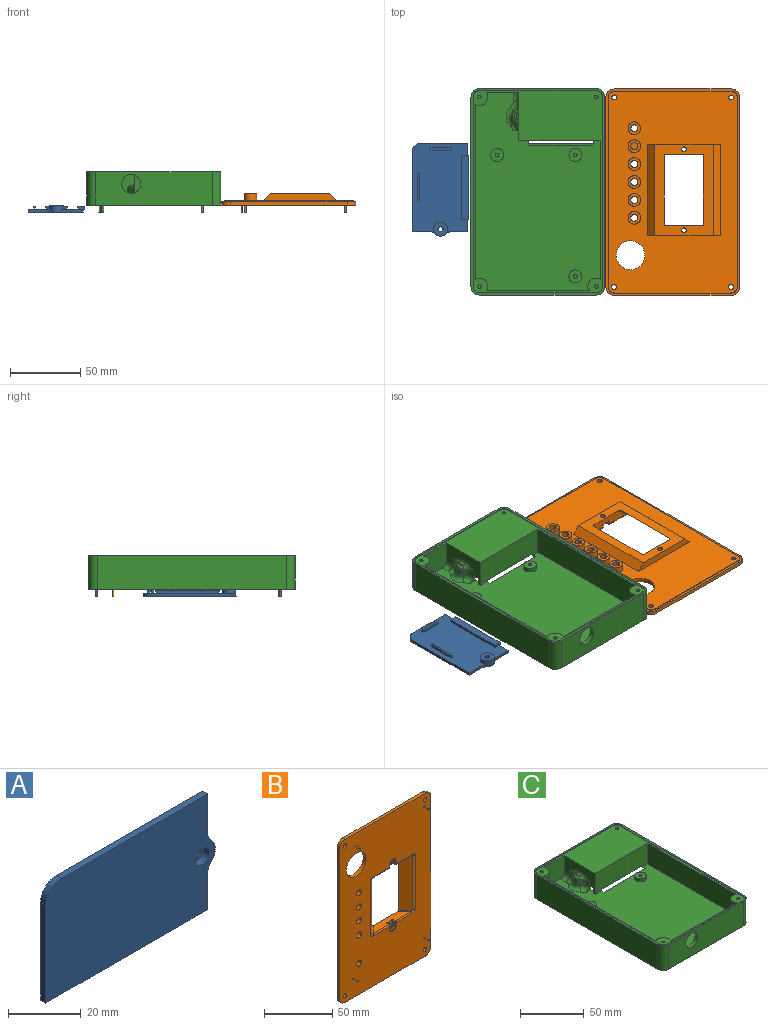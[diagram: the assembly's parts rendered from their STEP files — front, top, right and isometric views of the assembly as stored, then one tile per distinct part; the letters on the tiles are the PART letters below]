
ASSEMBLY  parts=3 mates=2
PART A: 31 faces, bbox 66x5x40 mm
  f0: plane 64.5x39mm, normal (0,1,0), area 2157.2mm2, adj f2,f3,f4,f5,f6,f7,f8,f9
  f1: cylinder r=1.75mm len=3.5mm, axis (0,-1,0), area 29.7mm2, adj f12,f13
  f2: cylinder r=5mm len=3.57mm, axis (0,1,0), area 8mm2, adj f0,f3,f10,f11
  f3: cylinder r=5mm len=10mm, axis (0,1,0), area 110.2mm2, adj f0,f2,f4,f11,f12
  f4: cylinder r=5mm len=3.57mm, axis (0,1,0), area 8mm2, adj f0,f3,f5,f11
  f5: plane 12.86x2mm, normal (1,0,0), area 25.7mm2, adj f0,f4,f6,f11
  f6: plane 57x2mm, normal (0,0,1), area 114mm2, adj f0,f5,f7,f11
  f7: cylinder r=6mm len=6mm, axis (0,1,0), area 18.8mm2, adj f0,f6,f8,f11
  f8: plane 33x2mm, normal (-1,0,0), area 66mm2, adj f0,f7,f9,f11
  f9: plane 63x2mm, normal (0,0,-1), area 126mm2, adj f0,f8,f10,f11,f25
  f10: plane 11.86x2mm, normal (1,0,0), area 23.7mm2, adj f0,f2,f9,f11
  f11: plane 66x39mm, normal (0,-1,0), area 2446.5mm2, adj f2,f3,f4,f5,f6,f7,f8,f9
  f12: plane 10x10mm, normal (0,1,0), area 68.9mm2, adj f1,f3
  f13: plane 5.55x5.55mm, normal (0,-1,0), area 14.6mm2, adj f1,f14
  f14: cylinder r=2.77mm len=5.55mm, axis (0,-1,0), area 40.1mm2, adj f11,f13
  f15: plane 2x1.25mm, normal (1,0,0), area 2.5mm2, adj f0,f16,f18,f19
  f16: plane 20x2mm, normal (0,0,-1), area 40mm2, adj f0,f15,f17,f19
  f17: plane 2x1.25mm, normal (-1,0,0), area 2.5mm2, adj f0,f16,f18,f19
  f18: plane 20x2mm, normal (0,0,1), area 40mm2, adj f0,f15,f17,f19
  f19: plane 20x1.25mm, normal (0,1,0), area 25mm2, adj f15,f16,f17,f18
  f20: plane 15x2mm, normal (-1,0,0), area 30mm2, adj f0,f21,f23,f24
  f21: plane 2x2mm, normal (0,0,1), area 4mm2, adj f0,f20,f22,f24
  f22: plane 15x2mm, normal (1,0,0), area 30mm2, adj f0,f21,f23,f24
  f23: plane 2x2mm, normal (0,0,-1), area 4mm2, adj f0,f20,f22,f24
  f24: plane 15x2mm, normal (0,1,0), area 30mm2, adj f20,f21,f22,f23
  f25: plane 45x0.95mm, normal (0,-1,0), area 42.8mm2, adj f9,f26,f27,f30
  f26: plane 4.95x2mm, normal (-1,0,0), area 9.9mm2, adj f0,f25,f28,f29,f30
  f27: plane 4.95x2mm, normal (1,0,0), area 9.9mm2, adj f0,f25,f28,f29,f30
  f28: plane 45x4.95mm, normal (0,1,0), area 222.7mm2, adj f26,f27,f29,f30
  f29: plane 45x2mm, normal (0,0,1), area 90mm2, adj f0,f26,f27,f28
  f30: plane 45x2mm, normal (0,0,-1), area 90mm2, adj f25,f26,f27,f28
PART B: 118 faces, bbox 95.4x14.1x146.9 mm
  f0: plane 143.15x91.65mm, normal (0,1,0), area 9009.7mm2, adj f22,f23,f25,f27,f29,f31,f33,f35
  f1: cylinder r=1mm len=15.99mm, axis (1,0,0), area 25.1mm2, adj f5,f19,f47,f70
  f2: cylinder r=1mm len=15.99mm, axis (-1,0,0), area 25.1mm2, adj f5,f20,f50,f82
  f3: cylinder r=1.75mm len=5mm, axis (0,-1,0), area 55mm2, adj f21,f59
  f4: cylinder r=1.75mm len=5mm, axis (0,-1,0), area 55mm2, adj f21,f53
  f5: plane 146.66x95.16mm, normal (0,-1,0), area 10918.9mm2, adj f1,f2,f6,f7,f8,f9,f10,f11
  f6: cylinder r=6mm len=6mm, axis (0,1,0), area 23.6mm2, adj f5,f7,f13,f93
  f7: plane 83x2.5mm, normal (0,0,1), area 207.5mm2, adj f5,f6,f8,f93
  f8: cylinder r=6mm len=6mm, axis (0,1,0), area 23.6mm2, adj f5,f7,f9,f93
  f9: plane 134.5x2.5mm, normal (-1,0,0), area 336.2mm2, adj f5,f8,f10,f93
  f10: cylinder r=6mm len=6mm, axis (0,1,0), area 23.6mm2, adj f5,f9,f11,f93
  f11: plane 83x2.5mm, normal (0,0,-1), area 207.5mm2, adj f5,f10,f12,f93
  f12: cylinder r=6mm len=6mm, axis (0,1,0), area 23.6mm2, adj f5,f11,f13,f93
  f13: plane 134.5x2.5mm, normal (1,0,0), area 336.2mm2, adj f5,f6,f12,f93
  f14: cylinder r=2.5mm len=8mm, axis (0,1,0), area 125.7mm2, adj f5,f32
  f15: cylinder r=2.5mm len=8mm, axis (0,1,0), area 125.7mm2, adj f5,f30
  f16: cylinder r=2.5mm len=8mm, axis (0,1,0), area 125.7mm2, adj f5,f28
  f17: cylinder r=2.5mm len=8mm, axis (0,1,0), area 125.7mm2, adj f5,f26
  f18: cylinder r=2.5mm len=8mm, axis (0,1,0), area 125.7mm2, adj f5,f24
  f19: plane 38.77x7mm, normal (0,0,-1), area 205.8mm2, adj f1,f21,f40,f44,f45,f64,f65,f66
  f20: plane 38.77x7mm, normal (0,0,1), area 205.8mm2, adj f2,f21,f42,f48,f51,f77,f78,f79
  f21: plane 65.22x42.02mm, normal (0,1,0), area 1275.6mm2, adj f3,f4,f19,f20,f22,f23,f38,f39
  f22: plane 51.6x5mm, normal (0,0,1), area 233mm2, adj f0,f21,f87,f88
  f23: plane 51.6x5mm, normal (0,0,-1), area 233mm2, adj f0,f21,f87,f88
  f24: plane 9x9mm, normal (0,1,0), area 44mm2, adj f18,f25
  f25: cylinder r=4.5mm len=9mm, axis (0,-1,0), area 141.4mm2, adj f0,f24
  f26: plane 9x9mm, normal (0,1,0), area 44mm2, adj f17,f27
  f27: cylinder r=4.5mm len=9mm, axis (0,-1,0), area 141.4mm2, adj f0,f26
  f28: plane 9x9mm, normal (0,1,0), area 44mm2, adj f16,f29
  f29: cylinder r=4.5mm len=9mm, axis (0,-1,0), area 141.4mm2, adj f0,f28
  f30: plane 9x9mm, normal (0,1,0), area 44mm2, adj f15,f31
  f31: cylinder r=4.5mm len=9mm, axis (0,-1,0), area 141.4mm2, adj f0,f30
  f32: plane 9x9mm, normal (0,1,0), area 44mm2, adj f14,f33
  f33: cylinder r=4.5mm len=9mm, axis (0,-1,0), area 141.4mm2, adj f0,f32
  f34: plane 9x9mm, normal (0,1,0), area 44mm2, adj f35,f36
  f35: cylinder r=4.5mm len=9mm, axis (0,-1,0), area 141.4mm2, adj f0,f34
  f36: cylinder r=2.5mm len=5mm, axis (0,-1,0), area 78.5mm2, adj f34,f37
  f37: plane 5x5mm, normal (0,1,0), area 19.6mm2, adj f36
  f38: plane 48.8x7.12mm, normal (-0.71,-0.71,0), area 491.5mm2, adj f21,f40,f42,f43
  f39: plane 48.8x7.12mm, normal (0.71,-0.71,0), area 491.5mm2, adj f21,f45,f49,f51
  f40: cylinder r=1mm len=8.54mm, axis (0.71,-0.71,0), area 15.7mm2, adj f19,f21,f38,f41
  f41: bspline ~3.66x2.02mm, area 6.2mm2, adj f5,f40,f43,f44
  f42: cylinder r=1mm len=8.54mm, axis (-0.71,0.71,0), area 15.7mm2, adj f20,f21,f38,f46
  f43: cylinder r=3mm len=48.8mm, axis (0,0,-1), area 115mm2, adj f5,f38,f41,f46
  f44: cylinder r=1mm len=15.99mm, axis (1,0,0), area 25.1mm2, adj f5,f19,f41,f69
  f45: cylinder r=1mm len=8.54mm, axis (0.71,0.71,0), area 15.7mm2, adj f19,f21,f39,f47
  f46: bspline ~3.66x2.02mm, area 6.2mm2, adj f5,f42,f43,f48
  f47: bspline ~3.66x2.02mm, area 6.2mm2, adj f1,f5,f45,f49
  f48: cylinder r=1mm len=15.99mm, axis (-1,0,0), area 25.1mm2, adj f5,f20,f46,f83
  f49: cylinder r=3mm len=48.8mm, axis (0,0,1), area 115mm2, adj f5,f39,f47,f50
  f50: bspline ~3.66x2.02mm, area 6.2mm2, adj f2,f5,f49,f51
  f51: cylinder r=1mm len=8.54mm, axis (-0.71,-0.71,0), area 15.7mm2, adj f20,f21,f39,f50
  f52: cylinder r=10.25mm len=20.5mm, axis (0,-1,0), area 193.2mm2, adj f0,f5
  f53: plane 5.25x4.8mm, normal (0,-1,0), area 13.1mm2, adj f4,f61,f62,f63,f64
  f54: plane 2.85x2mm, normal (-1,0,0), area 5.6mm2, adj f56,f62,f67,f69,f71
  f55: plane 2.85x2mm, normal (1,0,0), area 5.6mm2, adj f56,f63,f68,f70,f72
  f56: cylinder r=2.9mm len=5.8mm, axis (0,-1,0), area 18.2mm2, adj f54,f55,f61,f73
  f57: plane 2.85x2mm, normal (1,0,0), area 5.6mm2, adj f60,f75,f80,f82,f84
  f58: plane 2.85x2mm, normal (-1,0,0), area 5.6mm2, adj f60,f76,f81,f83,f85
  f59: plane 5.25x4.8mm, normal (0,-1,0), area 13.1mm2, adj f3,f74,f75,f76,f77
  f60: cylinder r=2.9mm len=5.8mm, axis (0,-1,0), area 18.2mm2, adj f57,f58,f74,f86
  f61: torus R=2.4mm, axis (0,-1,0), area 6.7mm2, adj f53,f56,f62,f63
  f62: cylinder r=0.5mm len=2.85mm, axis (0,0,1), area 2.2mm2, adj f53,f54,f61,f65
  f63: cylinder r=0.5mm len=2.85mm, axis (0,0,-1), area 2.2mm2, adj f53,f55,f61,f66
  f64: cylinder r=0.5mm len=4.8mm, axis (-1,0,0), area 3.8mm2, adj f19,f53,f65,f66
  f65: torus R=1mm, axis (0,0,1), area 0.8mm2, adj f19,f62,f64,f67
  f66: torus R=1mm, axis (0,0,1), area 0.8mm2, adj f19,f63,f64,f68
  f67: cylinder r=0.5mm len=1.5mm, axis (0,1,0), area 1.2mm2, adj f19,f54,f65,f69
  f68: cylinder r=0.5mm len=1.5mm, axis (0,-1,0), area 1.2mm2, adj f19,f55,f66,f70
  f69: torus R=0.5mm, axis (1,0,0), area 1mm2, adj f44,f54,f67,f71
  f70: torus R=0.5mm, axis (-1,0,0), area 1mm2, adj f1,f55,f68,f72
  f71: cylinder r=0.5mm len=2.35mm, axis (0,0,-1), area 1.8mm2, adj f5,f54,f69,f73
  f72: cylinder r=0.5mm len=2.35mm, axis (0,0,1), area 1.8mm2, adj f5,f55,f70,f73
  f73: torus R=3.4mm, axis (0,-1,0), area 7.6mm2, adj f5,f56,f71,f72
  f74: torus R=2.4mm, axis (0,-1,0), area 6.7mm2, adj f59,f60,f75,f76
  f75: cylinder r=0.5mm len=2.85mm, axis (0,0,-1), area 2.2mm2, adj f57,f59,f74,f78
  f76: cylinder r=0.5mm len=2.85mm, axis (0,0,1), area 2.2mm2, adj f58,f59,f74,f79
  f77: cylinder r=0.5mm len=4.8mm, axis (1,0,0), area 3.8mm2, adj f20,f59,f78,f79
  f78: torus R=1mm, axis (0,0,-1), area 0.8mm2, adj f20,f75,f77,f80
  f79: torus R=1mm, axis (0,0,-1), area 0.8mm2, adj f20,f76,f77,f81
  f80: cylinder r=0.5mm len=1.5mm, axis (0,1,0), area 1.2mm2, adj f20,f57,f78,f82
  f81: cylinder r=0.5mm len=1.5mm, axis (0,-1,0), area 1.2mm2, adj f20,f58,f79,f83
  f82: torus R=0.5mm, axis (-1,0,0), area 1mm2, adj f2,f57,f80,f84
  f83: torus R=0.5mm, axis (1,0,0), area 1mm2, adj f48,f58,f81,f85
  f84: cylinder r=0.5mm len=2.35mm, axis (0,0,1), area 1.8mm2, adj f5,f57,f82,f86
  f85: cylinder r=0.5mm len=2.35mm, axis (0,0,-1), area 1.8mm2, adj f5,f58,f83,f86
  f86: torus R=3.4mm, axis (0,-1,0), area 7.6mm2, adj f5,f60,f84,f85
  f87: plane 64.8x5mm, normal (0.71,0.71,0), area 458.2mm2, adj f0,f21,f22,f23
  f88: plane 64.8x5mm, normal (-0.71,0.71,0), area 458.2mm2, adj f0,f21,f22,f23
  f89: cylinder r=1.75mm len=3.5mm, axis (0,-1,0), area 33mm2, adj f0,f5
  f90: cylinder r=1.75mm len=3.5mm, axis (0,-1,0), area 33mm2, adj f0,f5
  f91: cylinder r=1.75mm len=3.5mm, axis (0,-1,0), area 33mm2, adj f0,f5
  f92: cylinder r=1.75mm len=3.5mm, axis (0,-1,0), area 33mm2, adj f0,f5
  f93: plane 146.5x95mm, normal (0,1,0), area 748.3mm2, adj f6,f7,f8,f9,f10,f11,f12,f13
  f94: plane 134.5x0.43mm, normal (-1,0,0), area 57.2mm2, adj f93,f95,f101,f109
  f95: cylinder r=4.4mm len=4.4mm, axis (0,-1,0), area 2.9mm2, adj f93,f94,f96,f108
  f96: plane 83x0.43mm, normal (0,0,-1), area 35.3mm2, adj f93,f95,f97,f106
  f97: cylinder r=4.4mm len=4.4mm, axis (0,-1,0), area 2.9mm2, adj f93,f96,f98,f104
  f98: plane 134.5x0.43mm, normal (1,0,0), area 57.2mm2, adj f93,f97,f99,f102
  f99: cylinder r=4.4mm len=4.4mm, axis (0,-1,0), area 2.9mm2, adj f93,f98,f100,f103
  f100: plane 83x0.43mm, normal (0,0,1), area 35.3mm2, adj f93,f99,f101,f105
  f101: cylinder r=4.4mm len=4.4mm, axis (0,-1,0), area 2.9mm2, adj f93,f94,f100,f107
  f102: plane 134.5x0.08mm, normal (0.71,0.71,0), area 14.3mm2, adj f0,f98,f103,f104
  f103: cone r=4.4mm half-angle=45deg, axis (0,-1,0), area 0.7mm2, adj f0,f99,f102,f105
  f104: cone r=4.4mm half-angle=45deg, axis (0,-1,0), area 0.7mm2, adj f0,f97,f102,f106
  f105: plane 83x0.08mm, normal (0,0.71,0.71), area 8.8mm2, adj f0,f100,f103,f107
  f106: plane 83x0.08mm, normal (0,0.71,-0.71), area 8.8mm2, adj f0,f96,f104,f108
  f107: cone r=4.4mm half-angle=45deg, axis (0,-1,0), area 0.7mm2, adj f0,f101,f105,f109
  f108: cone r=4.4mm half-angle=45deg, axis (0,-1,0), area 0.7mm2, adj f0,f95,f106,f109
  f109: plane 134.5x0.08mm, normal (-0.71,0.71,0), area 14.3mm2, adj f0,f94,f107,f108
  f110: cylinder r=0.5mm len=5mm, axis (0,1,0), area 15.7mm2, adj f5,f111
  f111: plane 1x1mm, normal (0,-1,0), area 0.8mm2, adj f110
  f112: cylinder r=0.5mm len=5mm, axis (0,1,0), area 15.7mm2, adj f5,f113
  f113: plane 1x1mm, normal (0,-1,0), area 0.8mm2, adj f112
  f114: cylinder r=0.5mm len=5mm, axis (0,1,0), area 15.7mm2, adj f5,f115
  f115: plane 1x1mm, normal (0,-1,0), area 0.8mm2, adj f114
  f116: cylinder r=0.5mm len=5mm, axis (0,1,0), area 15.7mm2, adj f5,f117
  f117: plane 1x1mm, normal (0,-1,0), area 0.8mm2, adj f116
PART C: 130 faces, bbox 95.4x146.9x28.9 mm
  f0: cylinder r=1mm len=11.36mm, axis (0,-1,0), area 14.4mm2, adj f1,f46,f47,f104
  f1: cylinder r=10mm len=19mm, axis (0,0,-1), area 112.7mm2, adj f0,f11,f41,f46,f47,f69,f70,f88
  f2: cylinder r=10mm len=19mm, axis (0,0,-1), area 112.7mm2, adj f3,f4,f10,f11,f46,f68,f70,f86
  f3: cylinder r=1mm len=9.36mm, axis (0,-1,0), area 11.3mm2, adj f2,f4,f46,f100
  f4: plane 18x6mm, normal (1,0,0), area 71mm2, adj f2,f3,f10,f13,f48,f56,f57,f97
  f5: plane 143.5x92mm, normal (0,0,1), area 2846mm2, adj f14,f15,f22,f23,f39,f40,f73,f75
  f6: cylinder r=3mm len=13.45mm, axis (0,0,-1), area 63.4mm2, adj f41,f49,f50,f83
  f7: cylinder r=3mm len=8mm, axis (0,0,1), area 37.7mm2, adj f13,f15,f22,f78
  f8: cylinder r=3mm len=8mm, axis (0,0,1), area 37.7mm2, adj f13,f14,f23,f76
  f9: cylinder r=3mm len=8mm, axis (0,0,1), area 37.7mm2, adj f13,f22,f23,f74
  f10: plane 14.12x9.54mm, normal (0,0,-1), area 75.3mm2, adj f2,f4,f44,f45,f48,f53,f66,f86
  f11: cylinder r=5mm len=15.9mm, axis (0,0,-1), area 102.3mm2, adj f1,f2,f46,f70
  f12: cylinder r=6mm len=21.5mm, axis (0,0,1), area 202.6mm2, adj f25,f26,f41,f113
  f13: plane 140.5x89mm, normal (0,0,1), area 10031.1mm2, adj f4,f7,f8,f9,f14,f15,f16,f18
  f14: plane 103.5x20mm, normal (-1,0,0), area 2007.6mm2, adj f5,f8,f13,f40,f75,f76
  f15: plane 28x20mm, normal (0,-1,0), area 494.2mm2, adj f5,f7,f13,f39,f65,f77,f78
  f16: cylinder r=4.6mm len=9.2mm, axis (0,0,-1), area 86.7mm2, adj f13,f17
  f17: plane 9.2x9.2mm, normal (0,0,1), area 61.2mm2, adj f16,f37
  f18: cylinder r=4.6mm len=9.2mm, axis (0,0,-1), area 86.7mm2, adj f13,f19
  f19: plane 9.2x9.2mm, normal (0,0,1), area 61.2mm2, adj f18,f35
  f20: cylinder r=4.6mm len=9.2mm, axis (0,0,-1), area 86.7mm2, adj f13,f21
  f21: plane 9.2x9.2mm, normal (0,0,1), area 61.2mm2, adj f20,f33
  f22: plane 134.5x20mm, normal (1,0,0), area 2565.3mm2, adj f5,f7,f9,f13,f73,f74,f77,f78
  f23: plane 83x20mm, normal (0,1,0), area 1394.3mm2, adj f5,f8,f9,f13,f29,f73,f74,f75
  f24: plane 146.5x95mm, normal (0,0,-1), area 11409.4mm2, adj f25,f26,f27,f28,f30,f31,f32,f42
  f25: plane 83x23.5mm, normal (0,1,0), area 1836.5mm2, adj f12,f24,f30,f41,f42,f113
  f26: plane 134.5x23.5mm, normal (1,0,0), area 3094.8mm2, adj f12,f24,f32,f41,f45,f113
  f27: plane 83x23.5mm, normal (0,-1,0), area 1809.5mm2, adj f24,f29,f31,f32,f113
  f28: plane 134.5x23.5mm, normal (-1,0,0), area 3160.8mm2, adj f24,f30,f31,f113
  f29: cylinder r=6.7mm len=13.4mm, axis (0,-1,0), area 126.3mm2, adj f23,f27
  f30: cylinder r=6mm len=23.5mm, axis (0,0,1), area 221.5mm2, adj f24,f25,f28,f113
  f31: cylinder r=6mm len=23.5mm, axis (0,0,1), area 221.5mm2, adj f24,f27,f28,f113
  f32: cylinder r=6mm len=23.5mm, axis (0,0,1), area 221.5mm2, adj f24,f26,f27,f113
  f33: cylinder r=1.3mm len=5mm, axis (0,0,1), area 40.8mm2, adj f21,f34
  f34: plane 2.6x2.6mm, normal (0,0,1), area 5.3mm2, adj f33
  f35: cylinder r=1.3mm len=5mm, axis (0,0,1), area 40.8mm2, adj f19,f36
  f36: plane 2.6x2.6mm, normal (0,0,1), area 5.3mm2, adj f35
  f37: cylinder r=1.3mm len=5mm, axis (0,0,1), area 40.8mm2, adj f17,f38
  f38: plane 2.6x2.6mm, normal (0,0,1), area 5.3mm2, adj f37
  f39: plane 34x20mm, normal (-1,0,0), area 373mm2, adj f5,f13,f15,f40,f48,f57,f60,f61
  f40: plane 58x20mm, normal (0,-1,0), area 1114mm2, adj f5,f13,f14,f39,f52,f53,f54
  f41: plane 63.54x39mm, normal (0,0,-1), area 358.9mm2, adj f1,f6,f12,f25,f26,f42,f45,f47
  f42: plane 12.86x2mm, normal (1,0,0), area 25.7mm2, adj f24,f25,f41,f67
  f43: cylinder r=5mm len=10mm, axis (0,0,-1), area 60.7mm2, adj f24,f66,f67,f68,f69,f70,f87,f89
  f44: plane 11.86x2mm, normal (1,0,0), area 23.7mm2, adj f10,f24,f45,f66
  f45: plane 63x2mm, normal (0,1,0), area 126mm2, adj f10,f24,f26,f41,f44,f51
  f46: plane 54x30mm, normal (0,0,-1), area 1540.4mm2, adj f0,f1,f2,f3,f11,f98,f99,f101
  f47: plane 18x7mm, normal (1,0,0), area 126mm2, adj f0,f1,f41,f102
  f48: plane 57x18mm, normal (0,1,0), area 896mm2, adj f4,f10,f13,f39,f41,f52,f53,f54
  f49: plane 28x18mm, normal (-1,0,0), area 467.2mm2, adj f6,f41,f81,f82,f95,f99
  f50: plane 52x18mm, normal (0,-1,0), area 899.2mm2, adj f6,f41,f84,f85,f102,f106
  f51: plane 46x1mm, normal (0,0,1), area 46mm2, adj f45,f53,f54,f55
  f52: plane 46x2mm, normal (0,0,-1), area 92mm2, adj f40,f48,f53,f54
  f53: plane 5x2mm, normal (1,0,0), area 7mm2, adj f10,f13,f40,f48,f51,f52,f55
  f54: plane 5x2mm, normal (-1,0,0), area 7mm2, adj f13,f40,f41,f48,f51,f52,f55
  f55: plane 46x1mm, normal (0,1,0), area 46mm2, adj f13,f51,f53,f54
  f56: plane 6.54x5.42mm, normal (0,-1,0), area 13.8mm2, adj f4,f13,f57,f61,f62
  f57: plane 5x3.07mm, normal (0,0,-1), area 10.2mm2, adj f4,f39,f48,f56,f61,f97
  f58: cylinder r=5mm len=7.45mm, axis (0,0,-1), area 42.1mm2, adj f60,f61,f63,f108
  f59: plane 4.47x1mm, normal (0,0,1), area 3.1mm2, adj f108,f111
  f60: cylinder r=10mm len=7.45mm, axis (0,0,-1), area 42.1mm2, adj f39,f58,f64,f107
  f61: cylinder r=10mm len=7.45mm, axis (0,0,-1), area 40.9mm2, adj f39,f56,f57,f58,f62,f109
  f62: torus R=6mm, axis (0,0,1), area 36.8mm2, adj f13,f56,f61,f63
  f63: torus R=9mm, axis (0,0,1), area 68.2mm2, adj f13,f58,f62,f64
  f64: torus R=6mm, axis (0,0,1), area 45.2mm2, adj f13,f60,f63,f65
  f65: cylinder r=4mm len=5.82mm, axis (0,-1,0), area 36.6mm2, adj f13,f15,f39,f64
  f66: cylinder r=5mm len=3.57mm, axis (0,0,-1), area 8.4mm2, adj f10,f24,f43,f44,f87
  f67: cylinder r=5mm len=3.57mm, axis (0,0,-1), area 8.4mm2, adj f24,f41,f42,f43,f89
  f68: plane 2.84x2.6mm, normal (0,1,0), area 7.4mm2, adj f2,f43,f70,f86
  f69: plane 2.84x2.6mm, normal (0,-1,0), area 7.4mm2, adj f1,f43,f70,f88
  f70: plane 10x10mm, normal (0,0,-1), area 75.5mm2, adj f1,f2,f11,f43,f68,f69,f72
  f71: plane 2.6x2.6mm, normal (0,0,-1), area 5.3mm2, adj f72
  f72: cylinder r=1.3mm len=6.9mm, axis (0,0,-1), area 56.4mm2, adj f70,f71
  f73: cylinder r=6mm len=12mm, axis (0,0,1), area 188.5mm2, adj f5,f22,f23,f74
  f74: plane 9x9mm, normal (0,0,-1), area 64.5mm2, adj f9,f22,f23,f73,f92
  f75: cylinder r=6mm len=12mm, axis (0,0,1), area 188.5mm2, adj f5,f14,f23,f76
  f76: plane 9x9mm, normal (0,0,-1), area 64.5mm2, adj f8,f14,f23,f75,f91
  f77: cylinder r=6mm len=12mm, axis (0,0,1), area 188.5mm2, adj f5,f15,f22,f78
  f78: plane 9x9mm, normal (0,0,-1), area 64.5mm2, adj f7,f15,f22,f77,f90
  f79: plane 2.22x2.22mm, normal (0,0,-1), area 3.3mm2, adj f80,f82,f84
  f80: torus R=3.37mm, axis (0,0,-1), area 14.9mm2, adj f79,f81,f85,f103
  f81: bspline ~8.03x6.57mm, area 30.1mm2, adj f49,f80,f82,f101
  f82: cylinder r=4mm len=4mm, axis (0,1,0), area 17.1mm2, adj f49,f79,f81,f83
  f83: bspline ~4.23x4mm, area 13.1mm2, adj f6,f82,f84
  f84: cylinder r=4mm len=4mm, axis (-1,0,0), area 17.1mm2, adj f50,f79,f83,f85
  f85: bspline ~8.03x6.57mm, area 30.1mm2, adj f50,f80,f84,f105
  f86: cylinder r=0.5mm len=2.84mm, axis (1,0,0), area 2.1mm2, adj f2,f10,f68,f87
  f87: torus R=5.5mm, axis (0,0,-1), area 2.5mm2, adj f10,f43,f66,f86
  f88: cylinder r=0.5mm len=2.84mm, axis (-1,0,0), area 2.1mm2, adj f1,f41,f69,f89
  f89: torus R=5.5mm, axis (0,0,-1), area 2.5mm2, adj f41,f43,f67,f88
  f90: cylinder r=1.3mm len=12mm, axis (0,0,1), area 98mm2, adj f5,f78
  f91: cylinder r=1.3mm len=12mm, axis (0,0,1), area 98mm2, adj f5,f76
  f92: cylinder r=1.3mm len=12mm, axis (0,0,1), area 98mm2, adj f5,f74
  f93: cylinder r=1.3mm len=3mm, axis (0,0,1), area 24.5mm2, adj f5,f94
  f94: plane 2.6x2.6mm, normal (0,0,1), area 5.3mm2, adj f93
  f95: cylinder r=1mm len=18mm, axis (0,0,1), area 28.3mm2, adj f41,f48,f49,f96
  f96: sphere r=1mm, area 1mm2, adj f95,f98,f99
  f97: cylinder r=1mm len=12mm, axis (0,0,1), area 18.8mm2, adj f4,f48,f57,f100
  f98: cylinder r=1mm len=54mm, axis (1,0,0), area 84.8mm2, adj f46,f48,f96,f100
  f99: cylinder r=1mm len=18.12mm, axis (0,1,0), area 28.5mm2, adj f46,f49,f96,f101
  f100: sphere r=1mm, area 2.1mm2, adj f3,f97,f98
  f101: bspline ~5.16x4.42mm, area 6.8mm2, adj f46,f81,f99,f103
  f102: cylinder r=1mm len=18mm, axis (0,0,1), area 28.3mm2, adj f41,f47,f50,f104
  f103: torus R=6.54mm, axis (0,0,1), area 7.5mm2, adj f46,f80,f101,f105
  f104: sphere r=1mm, area 2.1mm2, adj f0,f102,f106
  f105: bspline ~5.16x4.42mm, area 6.8mm2, adj f46,f85,f103,f106
  f106: cylinder r=1mm len=42.12mm, axis (-1,0,0), area 66.2mm2, adj f46,f50,f104,f105
  f107: torus R=12mm, axis (0,0,-1), area 13.7mm2, adj f60,f108,f110
  f108: torus R=3mm, axis (0,0,-1), area 22.6mm2, adj f58,f59,f107,f109
  f109: torus R=12mm, axis (0,0,-1), area 13.7mm2, adj f61,f108,f112
  f110: bspline ~10.29x4mm, area 10mm2, adj f39,f107,f111
  f111: cylinder r=2mm len=4.47mm, axis (0,-1,0), area 14mm2, adj f39,f59,f110,f112
  f112: bspline ~10.29x4mm, area 10mm2, adj f39,f109,f111
  f113: plane 146.5x95mm, normal (0,0,1), area 702mm2, adj f12,f25,f26,f27,f28,f30,f31,f32
  f114: plane 134.5x0.5mm, normal (1,0,0), area 67.3mm2, adj f5,f113,f115,f121
  f115: cylinder r=4.5mm len=4.5mm, axis (0,0,1), area 3.5mm2, adj f5,f113,f114,f116
  f116: plane 83x0.5mm, normal (0,1,0), area 41.5mm2, adj f5,f113,f115,f117
  f117: cylinder r=4.5mm len=4.5mm, axis (0,0,1), area 3.5mm2, adj f5,f113,f116,f118
  f118: plane 134.5x0.5mm, normal (-1,0,0), area 67.3mm2, adj f5,f113,f117,f119
  f119: cylinder r=4.5mm len=4.5mm, axis (0,0,1), area 3.5mm2, adj f5,f113,f118,f120
  f120: plane 83x0.5mm, normal (0,-1,0), area 41.5mm2, adj f5,f113,f119,f121
  f121: cylinder r=4.5mm len=4.5mm, axis (0,0,1), area 3.5mm2, adj f5,f113,f114,f120
  f122: cylinder r=0.72mm len=5mm, axis (0,0,1), area 22.6mm2, adj f24,f123
  f123: plane 1.44x1.44mm, normal (0,0,-1), area 1.6mm2, adj f122
  f124: cylinder r=0.72mm len=5mm, axis (0,0,1), area 22.6mm2, adj f24,f125
  f125: plane 1.44x1.44mm, normal (0,0,-1), area 1.6mm2, adj f124
  f126: cylinder r=0.72mm len=5mm, axis (0,0,1), area 22.6mm2, adj f24,f127
  f127: plane 1.44x1.44mm, normal (0,0,-1), area 1.6mm2, adj f126
  f128: cylinder r=0.72mm len=5mm, axis (0,0,1), area 22.6mm2, adj f24,f129
  f129: plane 1.44x1.44mm, normal (0,0,-1), area 1.6mm2, adj f128
PLACE A rot(axis=(0.58,-0.58,-0.58),120deg) t=(-14.8,-129.49,-1.75)mm
PLACE B rot(axis=(1,0,0),90deg) t=(-3.33,-16.74,4.25)mm
PLACE C t=(-99.03,-150,7.25)mm fixed
MATE planar C.f24 <-> B.f5  axis (0,0,-1) through (-69.12,-94.87,1.25)mm
MATE planar A.f11 <-> C.f124  axis (0,0,-1) through (-135.24,-80.28,-3.75)mm
